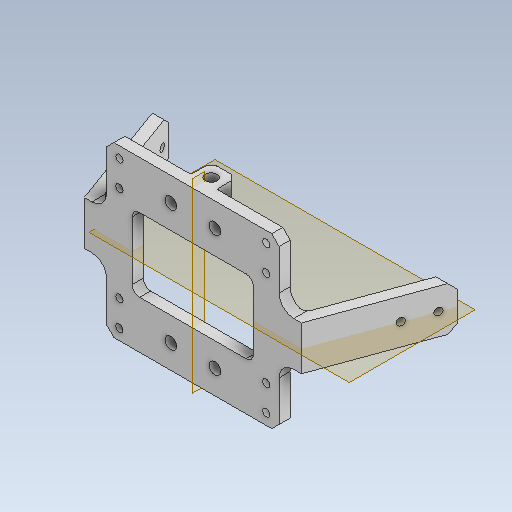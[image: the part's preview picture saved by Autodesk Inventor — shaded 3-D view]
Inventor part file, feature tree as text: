
AUTODESK INVENTOR PART (.ipt)
format: ipt  version: 2020 (Build 240168000, 168)  size: 404,480 bytes
history: native  units: mm
features: other x15, reference x14, sketch x8, extrude x7, projected_geometry x7, fillet x6, mirror x4, chamfer x3, plane x2, hole x1
ambient origin geometry x8: Origin, YZ Plane, XZ Plane, XY Plane, X Axis, Y Axis, Z Axis, Center Point
bodies: Solid1 (feature_tree)
feature tree (67):
  extrude  "Extrusion1"  Depth=12.0mm
  hole  "Hole1"  [1 undecoded]
  plane  "Work Plane1"
  extrude  "Extrusion2"  Depth=19.198622mm
  extrude  "Extrusion3"  Depth=3.0mm TaperAngle=0.0deg
  plane  "Work Plane2"
  extrude  "Extrusion4"  Depth=2.0mm TaperAngle=0.0deg
  mirror  "Mirror1"
  extrude  "Extrusion5"  Depth=6.0mm
  mirror  "Mirror2"
  extrude  "Extrusion6"  Depth=1.0mm
  mirror  "Mirror3"
  chamfer  "Chamfer1"  Distance=6.0mm
  fillet  "Fillet3"  Radius=2.0mm
  fillet  "Fillet4"  Radius=7.0mm
  fillet  "Fillet5"  Radius=7.0mm
  fillet  "Fillet6"  Radius=3.2mm
  fillet  "Fillet7"  Radius=6.0mm
  fillet  "Fillet8"  Radius=1.5mm
  chamfer  "Chamfer2"  Distance=2.0mm
  extrude  "Extrusion7"  Depth=1.0mm
  mirror  "Mirror4"
  chamfer  "Chamfer3"  Distance=2.0mm
  sketch  "Sketch1"  dims[d0=3.0mm d1=0.0mm]
  reference  "Reference1"
  reference  "Reference2"
  reference  "Reference3"
  reference  "Reference4"
  sketch  "Sketch2"  dims[d2=2.0mm d3=6.0mm d4=4.0mm d5=2.0mm d6=90.0deg d7=20.0mm d8=0.0mm d9=12.0mm]
  reference  "Reference5"
  reference  "Reference6"
  reference  "Reference7"
  reference  "Reference8"
  reference  "Reference9"
  reference  "Reference10"
  reference  "Reference11"
  reference  "Reference12"
  sketch  "Sketch3"  dims[d10=8.0mm d11=3.0mm d12=0.0mm]
  projected_geometry  "Projected Loop1"
  sketch  "Sketch4"  dims[d13=30.0mm d14=19.198622mm]
  projected_geometry  "Projected Loop2"
  sketch  "Sketch5"  dims[d15=3.0mm d16=3.0mm d17=0.0mm]
  projected_geometry  "Projected Loop3"
  projected_geometry  "Projected Loop4"
  sketch  "Sketch6"  dims[d19=15.0mm d20=2.0mm d21=0.0mm]
  projected_geometry  "Projected Loop5"
  projected_geometry  "Projected Loop6"
  sketch  "Sketch7"  dims[d23=6.0mm d24=6.0mm]
  projected_geometry  "Projected Loop7"
  sketch  "Sketch8"  dims[d25=3.2mm d26=3.2mm d27=6.0mm d28=0.0mm d29=2.0mm d30=7.0mm d31=7.0mm d32=3.2mm d33=6.0mm d34=0.0mm d35=1.5mm d36=2.0mm d37=45.0deg d38=2.0mm d39=0.5mm d40=2.0mm d41=2.0mm d42=4.0mm d43=1.0mm d44=2.0mm d45=2.0mm d46=45.0deg d47=2.0mm d48=2.0mm d49=6.0mm d50=0.0mm d51=2.0mm d52=2.0mm d53=45.0deg]
  reference  "Reference13"
  reference  "Reference14"
  parser-record x1  (decoder bookkeeping rows leaked as tree rows — omitted from the tree; the rows remain in map.json)
  other  "body_1.iam"
  other  "leg_1_MIR:2"
  other  "reducer_1_MIR:3"
  other  "mot_holder_1_MIR:1"
  other  "leg_1:1"
  other  "reducer_1:3"
  other  "mot_holder_1:1"
  other  "leg_1:2"
  other  "leg_1_MIR:1"
  other  "screw_holder_2_3_MIR:5"
  other  "screw_holder_2_3_MIR:4"
  other  "screw_holder_2_3:14"
  other  "screw_holder_2_3:15"
  other  "body_shell_1:1"
note: 1 required parameter value undecoded (feature->parameter linkage not recoverable at this tier; creation-order binding heuristic only, values carry confidence <= 0.55)
note: 1 file-system path scrubbed to <path> (originals preserved in map.json)
